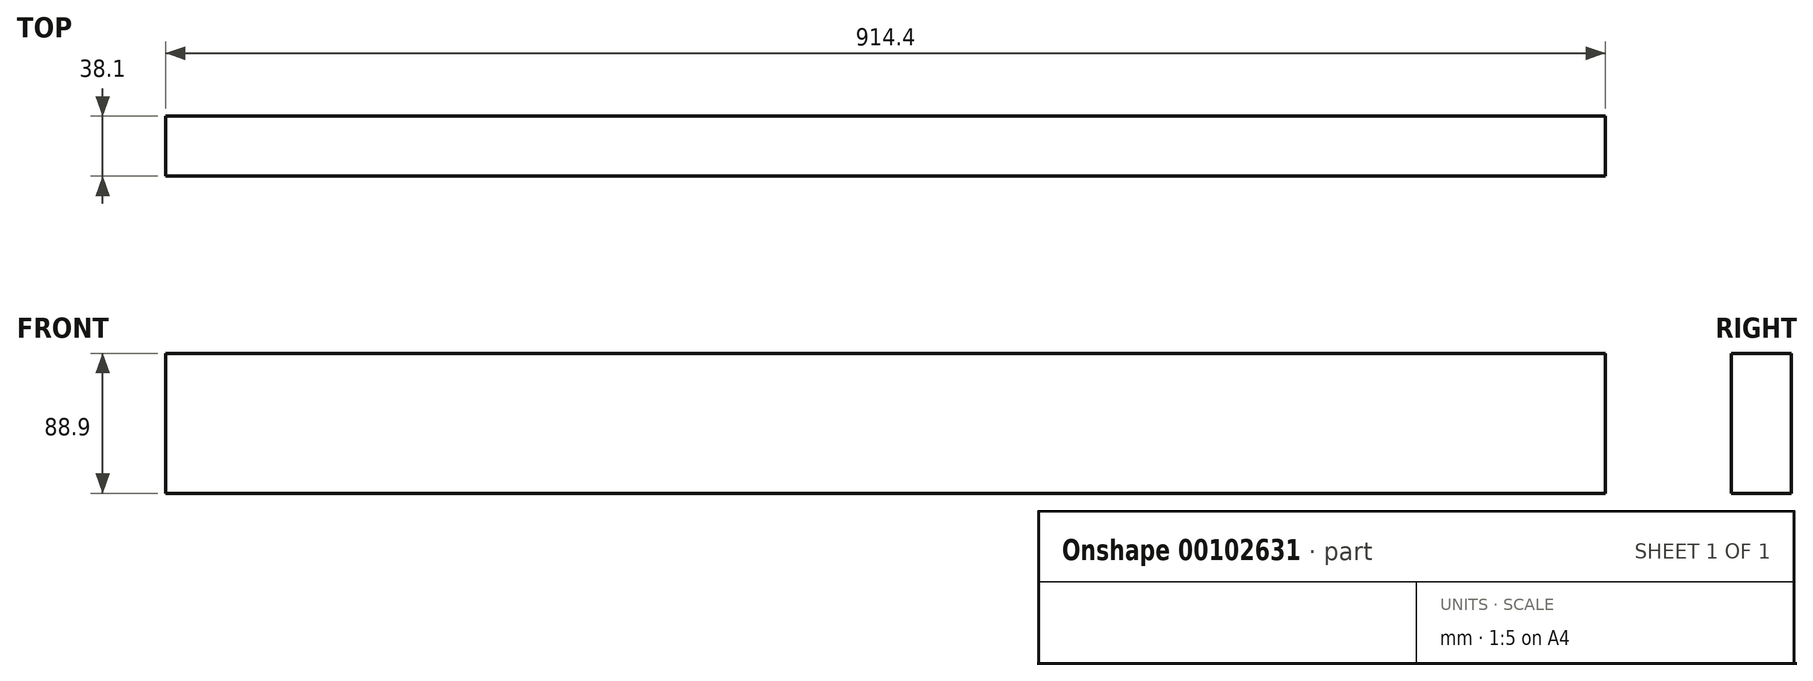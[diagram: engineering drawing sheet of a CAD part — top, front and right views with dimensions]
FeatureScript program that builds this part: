
annotation { "Feature Type Name" : "Feature", "Feature Type Description" : "" }
export const myFeature = defineFeature(function(context is Context, id is Id, definition is map)
    precondition{}
    {
        {
            var Q0;
            Q0=qCreatedBy(makeId("Right.planeOp"),FACE);
            var sketch = newSketch(context, id + "F0", { "sketchPlane" : qUnion([Q0])});
            skLineSegment(sketch, "E0.bottom", {"start": v(-42.58, 36.94) * mm, "end": v(-4.48, 36.94) * mm});
            skLineSegment(sketch, "E0.top", {"start": v(-42.58, -51.96) * mm, "end": v(-4.48, -51.96) * mm});
            skLineSegment(sketch, "E0.left", {"start": v(-42.58, 36.94) * mm, "end": v(-42.58, -51.96) * mm});
            skLineSegment(sketch, "E0.right", {"start": v(-4.48, 36.94) * mm, "end": v(-4.48, -51.96) * mm});
            skSolve(sketch);
        }
        {
            var Q0;
            Q0=makeQuery(id+"F0.imprint","IMPRINT",FACE,{"disambiguationData":[TD([[makeQuery(id+"F0.imprint","IMPRINT",EDGE,{"derivedFrom":sQuery(id+"F0.wireOp",EDGE,"E0.bottom")}),-1.0]])]});
            extrude(context, id + "F1", {"entities" : qUnion([Q0]), "depth" : 914.4 * mm});
        }
    });
